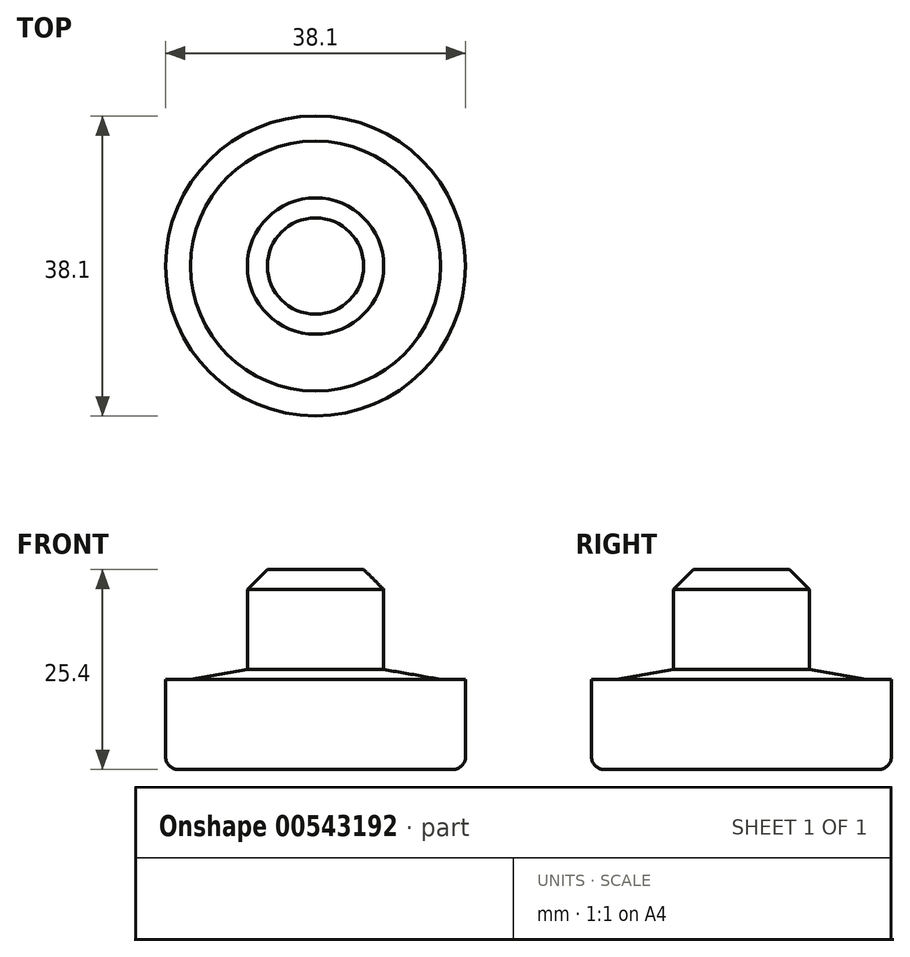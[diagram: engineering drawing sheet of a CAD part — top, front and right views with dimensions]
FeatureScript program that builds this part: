
annotation { "Feature Type Name" : "Feature", "Feature Type Description" : "" }
export const myFeature = defineFeature(function(context is Context, id is Id, definition is map)
    precondition{}
    {
        {
            var Q0;
            Q0=qCreatedBy(makeId("Front.planeOp"),FACE);
            var sketch = newSketch(context, id + "F0", { "sketchPlane" : qUnion([Q0])});
            skLineSegment(sketch, "E0", {"start": v(0, 14.96) * mm, "end": v(8.66, 14.96) * mm});
            skLineSegment(sketch, "E1", {"start": v(8.66, 14.96) * mm, "end": v(8.66, 2.26) * mm});
            skLineSegment(sketch, "E2", {"start": v(8.66, 2.26) * mm, "end": v(15.88, 1) * mm});
            skLineSegment(sketch, "E3", {"start": v(15.88, 1) * mm, "end": v(19.05, 1) * mm});
            skLineSegment(sketch, "E4", {"start": v(19.05, 1) * mm, "end": v(19.05, -10.44) * mm});
            skLineSegment(sketch, "E5", {"start": v(19.05, -10.44) * mm, "end": v(0, -10.44) * mm});
            skLineSegment(sketch, "E6", {"start": v(0, -10.44) * mm, "end": v(0, 14.96) * mm});
            skLineSegment(sketch, "E7", {"start": v(0, 26.06) * mm, "end": v(0, -22.4) * mm, "construction": true});
            skSolve(sketch);
        }
        {
            var Q0;
            Q0=makeQuery(id+"F0.imprint","IMPRINT",FACE,{"disambiguationData":[TD([[makeQuery(id+"F0.imprint","IMPRINT",EDGE,{"derivedFrom":sQuery(id+"F0.wireOp",EDGE,"E0")}),-1.0]])]});
            var Q1;
            Q1=sQuery(id+"F0.wireOp",EDGE,"E7");
            revolve(context, id + "F1", {"entities" : qUnion([Q0]), "axis" : qUnion([Q1]), "revolveType" : RevolveType.FULL});
        }
        {
            var Q0;
            Q0=makeQuery(id+"F1.opRevolve","SWEPT_EDGE",EDGE,{"disambiguationData":[OSD([sQuery(id+"F0.wireOp",EDGE,"E0"),sQuery(id+"F0.wireOp",EDGE,"E1")])]});
            chamfer(context, id + "F2", {"entities" : qUnion([Q0]), "width" : 2.54 * mm, "tangentPropagation" : true});
        }
        {
            var Q0;
            Q0=makeQuery(id+"F1.opRevolve","SWEPT_EDGE",EDGE,{"disambiguationData":[OSD([sQuery(id+"F0.wireOp",EDGE,"E4"),sQuery(id+"F0.wireOp",EDGE,"E5")])]});
            fillet(context, id + "F3", {"entities" : qUnion([Q0]), "radius" : 1.59 * mm, "tangentPropagation" : true, "allowEdgeOverflow" : false});
        }
    });
